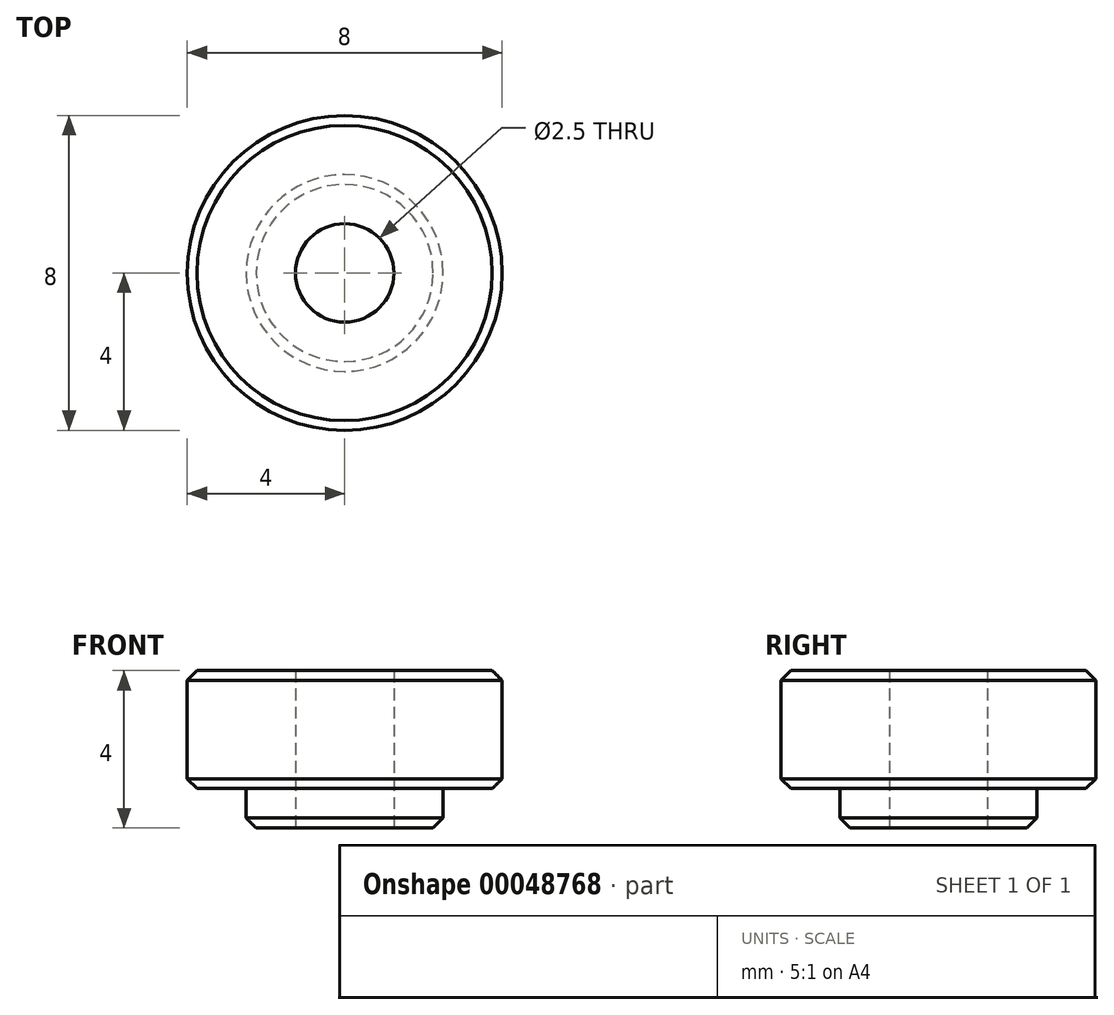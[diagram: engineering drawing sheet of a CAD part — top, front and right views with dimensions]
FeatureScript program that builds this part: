
annotation { "Feature Type Name" : "Feature", "Feature Type Description" : "" }
export const myFeature = defineFeature(function(context is Context, id is Id, definition is map)
    precondition{}
    {
        {
            var Q0;
            Q0=qCreatedBy(makeId("Top.planeOp"),FACE);
            var sketch = newSketch(context, id + "F0", { "sketchPlane" : qUnion([Q0])});
            skCircle(sketch, "E0", {"center": v(0, 0) * mm, "radius": 4 * mm});
            skSolve(sketch);
        }
        {
            var Q0;
            Q0=makeQuery(id+"F0.imprint","IMPRINT",FACE,{"disambiguationData":[TD([[makeQuery(id+"F0.imprint","IMPRINT",EDGE,{"derivedFrom":sQuery(id+"F0.wireOp",EDGE,"E0")}),1.0]])]});
            extrude(context, id + "F1", {"entities" : qUnion([Q0]), "oppositeDirection" : true, "depth" : 3 * mm});
        }
        {
            var Q0;
            Q0=makeQuery(id+"F1.opExtrude","CAP_FACE",FACE,{"disambiguationData":[OSD([sQuery(id+"F0.wireOp",EDGE,"E0")])],"isStart":false});
            var sketch = newSketch(context, id + "F2", { "sketchPlane" : qUnion([Q0])});
            skCircle(sketch, "E1", {"center": v(0, 0) * mm, "radius": 2.5 * mm});
            skSolve(sketch);
        }
        {
            var Q0;
            Q0=makeQuery(id+"F2.imprint","IMPRINT",FACE,{"disambiguationData":[TD([[makeQuery(id+"F2.imprint","IMPRINT",EDGE,{"derivedFrom":sQuery(id+"F2.wireOp",EDGE,"E1")}),1.0]])]});
            extrude(context, id + "F3", {"entities" : qUnion([Q0]), "operationType" : NewBodyOperationType.ADD, "depth" : 1 * mm});
        }
        {
            var Q0;
            Q0=makeQuery(id+"F1.opExtrude","CAP_FACE",FACE,{"disambiguationData":[OSD([sQuery(id+"F0.wireOp",EDGE,"E0")])],"isStart":true});
            var sketch = newSketch(context, id + "F4", { "sketchPlane" : qUnion([Q0])});
            skPoint(sketch, "E2.middle", {"position": v(0, 0) * mm});
            skSolve(sketch);
        }
        {
            var Q0;
            Q0=sQuery(id+"F4.wireOp",VERTEX,"E2.middle");
            var Q1;
            Q1=makeQuery(id+"F1.opExtrude","SWEPT_BODY",BODY,{"disambiguationData":[OSD([sQuery(id+"F0.wireOp",EDGE,"E0")])]});
            hole(context, id + "F5", {"style" : HoleStyle.SIMPLE, "endStyle" : HoleEndStyle.THROUGH, "standardTappedOrClearance" : lookupTablePath({ "standard" : "ISO", "engagement" : "75%", "pitch" : "0.5 mm", "size" : "M3", "type" : "Tapped" }), "standardBlindInLast" : lookupTablePath({ "fit" : "Normal", "standard" : "ISO", "engagement" : "75%", "pitch" : "0.5 mm", "size" : "M3", "type" : "Clearance & tapped" }), "holeDiameter" : 2.5 * mm, "majorDiameter" : 3 * mm, "showTappedDepth" : true, "isTappedThrough" : true, "tappedDepth" : 3 * mm, "tapClearance" : 3, "locations" : qUnion([Q0]), "scope" : qUnion([Q1]), "startStyle" : HoleStartStyle.PART});
        }
        {
            var Q0;
            Q0=makeQuery(id+"F1.opExtrude","CAP_EDGE",EDGE,{"disambiguationData":[OSD([sQuery(id+"F0.wireOp",EDGE,"E0")])],"isStart":true});
            var Q1;
            Q1=makeQuery(id+"F1.opExtrude","CAP_EDGE",EDGE,{"disambiguationData":[OSD([sQuery(id+"F0.wireOp",EDGE,"E0")])],"isStart":false});
            var Q2;
            Q2=makeQuery(id+"F5.hole-0.boolean.opBoolean","COPY",EDGE,{"derivedFrom":makeQuery(id+"F5.hole-0.opRevolve","SWEPT_EDGE",EDGE,{"disambiguationData":[OSD([sQuery(id+"F5.hole-0.sketch.wireOp",EDGE,"core_line_2"),sQuery(id+"F5.hole-0.sketch.wireOp",EDGE,"core_line_3")])]})});
            var Q3;
            Q3=makeQuery(id+"F3.opExtrude","CAP_EDGE",EDGE,{"disambiguationData":[OSD([sQuery(id+"F2.wireOp",EDGE,"E1")])],"isStart":false});
            chamfer(context, id + "F6", {"entities" : qUnion([Q0, Q1, Q2, Q3]), "width" : 0.25 * mm, "tangentPropagation" : true});
        }
    });
